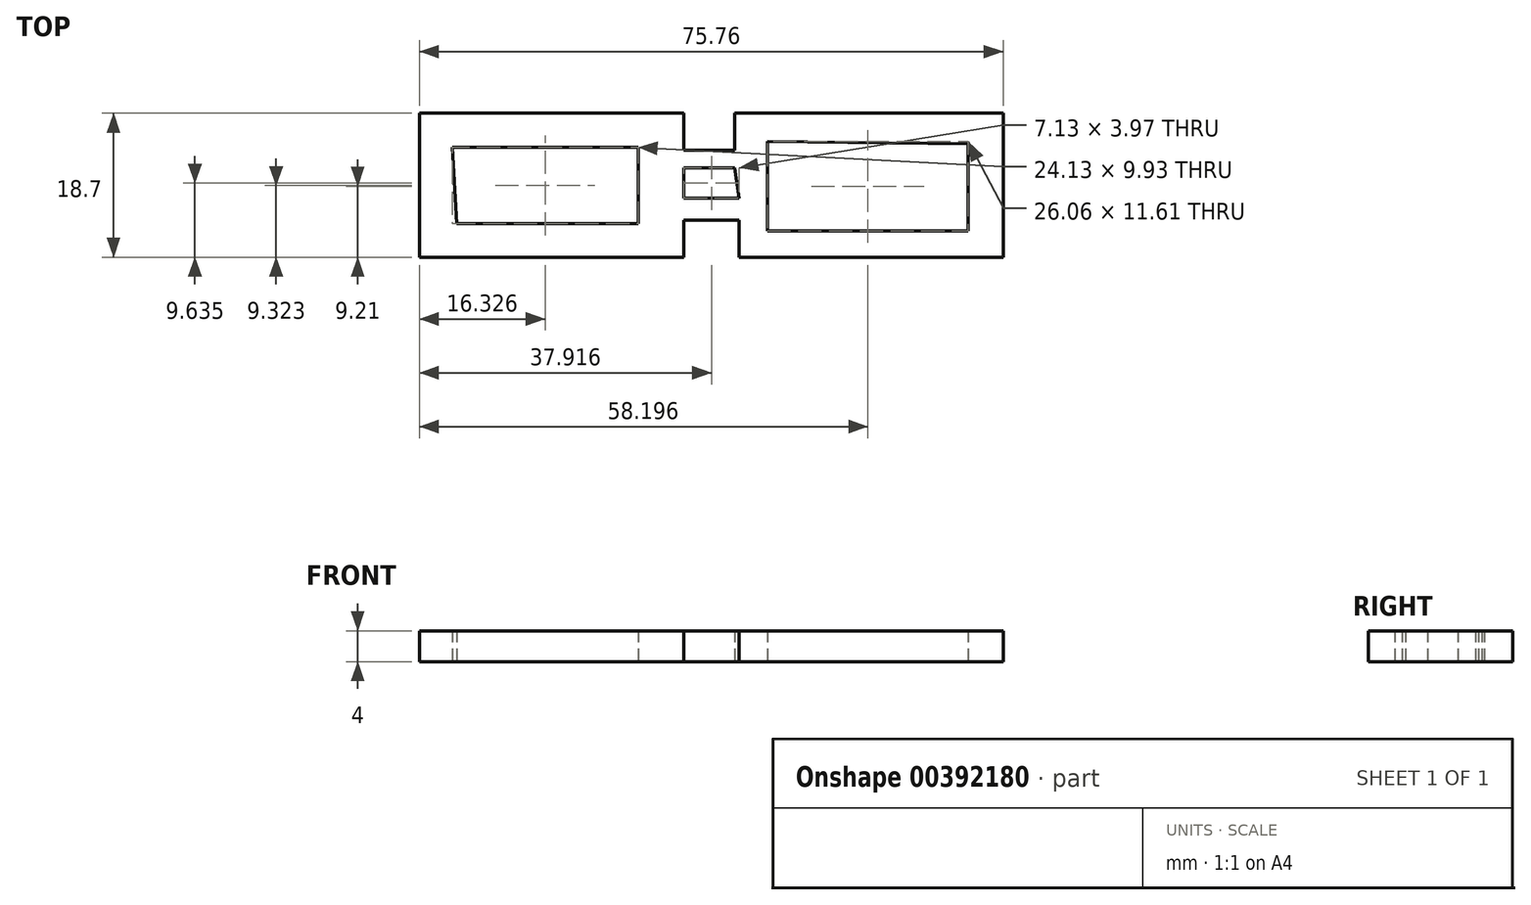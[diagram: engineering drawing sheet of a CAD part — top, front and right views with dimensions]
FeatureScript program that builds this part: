
annotation { "Feature Type Name" : "Feature", "Feature Type Description" : "" }
export const myFeature = defineFeature(function(context is Context, id is Id, definition is map)
    precondition{}
    {
        {
            var Q0;
            Q0=qCreatedBy(makeId("Top.planeOp"),FACE);
            var sketch = newSketch(context, id + "F0", { "sketchPlane" : qUnion([Q0])});
            skLineSegment(sketch, "E0", {"start": v(3.12, 0) * mm, "end": v(37.96, 0) * mm});
            skLineSegment(sketch, "E1", {"start": v(37.96, 0) * mm, "end": v(37.96, -18.7) * mm});
            skLineSegment(sketch, "E2", {"start": v(37.96, -18.7) * mm, "end": v(3.68, -18.7) * mm});
            skLineSegment(sketch, "E3", {"start": v(18.13, 0) * mm, "end": v(32.3, 0) * mm});
            skLineSegment(sketch, "E4", {"start": v(32.3, 0) * mm, "end": v(37.96, 0) * mm});
            skLineSegment(sketch, "E5", {"start": v(3.68, -18.7) * mm, "end": v(3.68, -13.88) * mm});
            skLineSegment(sketch, "E6", {"start": v(3.12, 0) * mm, "end": v(3.12, -4.82) * mm});
            skLineSegment(sketch, "E7", {"start": v(3.68, -13.88) * mm, "end": v(0, -13.88) * mm});
            skLineSegment(sketch, "E8", {"start": v(3.12, -4.82) * mm, "end": v(0, -4.82) * mm});
            skLineSegment(sketch, "E9", {"start": v(0, -13.88) * mm, "end": v(0, -11.05) * mm});
            skLineSegment(sketch, "E10", {"start": v(0, -4.82) * mm, "end": v(0, -7.08) * mm});
            skLineSegment(sketch, "E11", {"start": v(0, -11.05) * mm, "end": v(3.68, -11.05) * mm});
            skLineSegment(sketch, "E12", {"start": v(3.68, -11.05) * mm, "end": v(3.12, -7.08) * mm});
            skLineSegment(sketch, "E13", {"start": v(0, -7.08) * mm, "end": v(3.12, -7.08) * mm});
            skLineSegment(sketch, "E14", {"start": v(33.43, -3.97) * mm, "end": v(33.43, -15.3) * mm});
            skLineSegment(sketch, "E15", {"start": v(33.43, -15.3) * mm, "end": v(7.37, -15.3) * mm});
            skLineSegment(sketch, "E16", {"start": v(7.37, -15.3) * mm, "end": v(7.37, -3.68) * mm});
            skLineSegment(sketch, "E17", {"start": v(7.37, -3.68) * mm, "end": v(33.43, -3.97) * mm});
            skLineSegment(sketch, "E18", {"start": v(0, -4.82) * mm, "end": v(-3.45, -4.82) * mm});
            skLineSegment(sketch, "E19", {"start": v(0, -7.08) * mm, "end": v(-3.45, -7.08) * mm});
            skLineSegment(sketch, "E20", {"start": v(-3.45, -7.08) * mm, "end": v(-3.45, -4.82) * mm});
            skLineSegment(sketch, "E21", {"start": v(0, -11.05) * mm, "end": v(-3.45, -11.05) * mm});
            skLineSegment(sketch, "E22", {"start": v(-3.45, -11.05) * mm, "end": v(-3.45, -13.88) * mm});
            skLineSegment(sketch, "E23", {"start": v(-3.45, -13.88) * mm, "end": v(0, -13.88) * mm});
            skLineSegment(sketch, "E24", {"start": v(-6.86, 0) * mm, "end": v(-3.45, 0) * mm});
            skLineSegment(sketch, "E25", {"start": v(-3.45, 0) * mm, "end": v(-3.45, -18.7) * mm});
            skPoint(sketch, "E25.endSnap0", {"position": v(20.82, -18.7) * mm});
            skLineSegment(sketch, "E26", {"start": v(-3.45, -18.7) * mm, "end": v(-37.8, -18.7) * mm});
            skLineSegment(sketch, "E27", {"start": v(-37.8, -18.7) * mm, "end": v(-37.8, 0) * mm});
            skLineSegment(sketch, "E28", {"start": v(-37.8, 0) * mm, "end": v(-6.86, 0) * mm});
            skLineSegment(sketch, "E29", {"start": v(-33.54, -4.4) * mm, "end": v(-9.41, -4.4) * mm});
            skLineSegment(sketch, "E30", {"start": v(-9.41, -4.4) * mm, "end": v(-9.41, -14.34) * mm});
            skLineSegment(sketch, "E31", {"start": v(-9.41, -14.34) * mm, "end": v(-32.97, -14.34) * mm});
            skLineSegment(sketch, "E32", {"start": v(-32.97, -14.34) * mm, "end": v(-33.54, -4.4) * mm});
            skSolve(sketch);
        }
        {
            var Q0;
            Q0=makeQuery(id+"F0.imprint","IMPRINT",FACE,{"disambiguationData":[TD([[makeQuery(id+"F0.imprint","IMPRINT",EDGE,{"derivedFrom":sQuery(id+"F0.wireOp",EDGE,"E9")}),1.0]])]});
            var Q1;
            Q1=makeQuery(id+"F0.imprint","IMPRINT",FACE,{"disambiguationData":[TD([[makeQuery(id+"F0.imprint","IMPRINT",EDGE,{"derivedFrom":sQuery(id+"F0.wireOp",EDGE,"E10")}),-1.0]])]});
            var Q2;
            Q2=makeQuery(id+"F0.imprint","IMPRINT",FACE,{"disambiguationData":[TD([[makeQuery(id+"F0.imprint","IMPRINT",EDGE,{"derivedFrom":sQuery(id+"F0.wireOp",EDGE,"E0")}),-1.0]])]});
            var Q3;
            {var subQ4=sQuery(id+"F0.wireOp",EDGE,"E24");Q3=makeQuery(id+"F0.imprint","IMPRINT",FACE,{"disambiguationData":[TD([[makeQuery(id+"F0.imprint","IMPRINT",EDGE,{"derivedFrom":subQ4}),-1.0]])]});}
            extrude(context, id + "F1", {"entities" : qUnion([Q0, Q1, Q2, Q3]), "depth" : 4 * mm});
        }
    });
